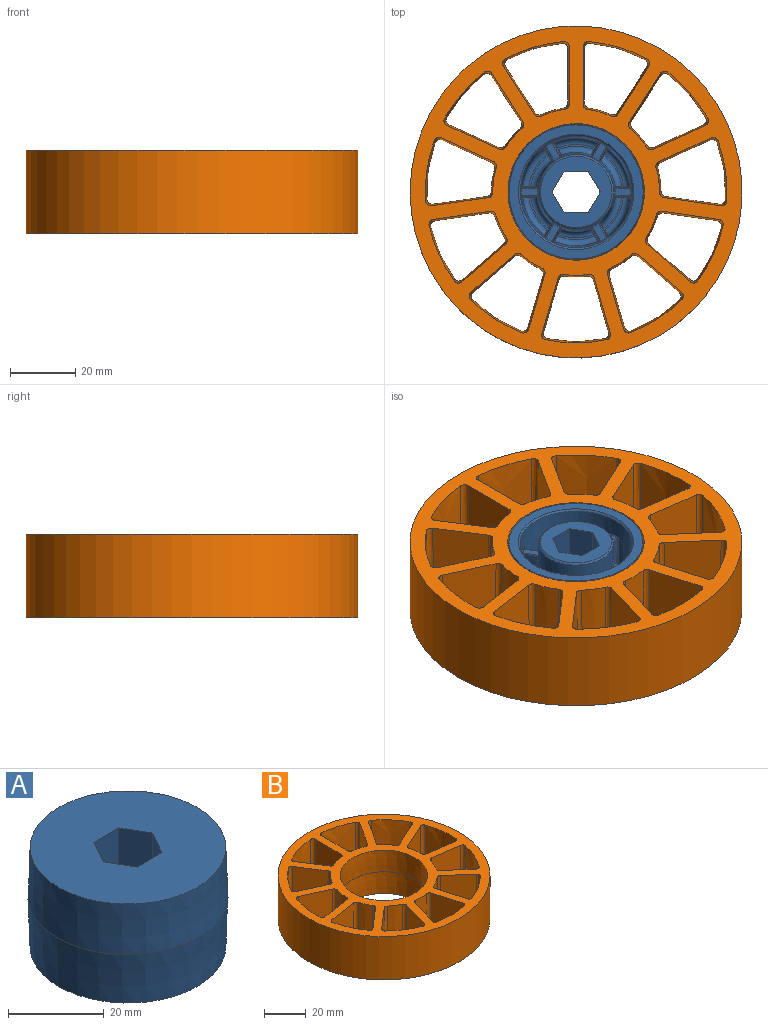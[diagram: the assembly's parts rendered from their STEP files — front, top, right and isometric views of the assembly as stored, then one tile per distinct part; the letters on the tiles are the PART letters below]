
ASSEMBLY  parts=2 mates=1
PART A: 159 faces, bbox 41.9x41.9x25.4 mm
  f0: torus R=16.68mm, axis (0,0,1), area 0.8mm2, adj f6,f31,f40,f45
  f1: torus R=11.9mm, axis (0,0,1), area 0.8mm2, adj f7,f31,f36,f41
  f2: cone r=20.24mm half-angle=2deg, axis (0,0,-1), area 1655.4mm2, adj f3,f25
  f3: cone r=20.96mm half-angle=2deg, axis (0,0,1), area 1655.4mm2, adj f2,f26
  f4: cone r=10.9mm half-angle=47deg, axis (0,0,1), area 52.3mm2, adj f7,f24
  f5: cone r=17.13mm half-angle=45deg, axis (0,0,-1), area 81.3mm2, adj f6,f26
  f6: cone r=16.46mm half-angle=2deg, axis (0,0,-1), area 1757.7mm2, adj f0,f5,f9,f12,f15,f18,f21,f27
  f7: cone r=11.43mm half-angle=2deg, axis (0,0,1), area 1163.6mm2, adj f1,f4,f8,f11,f14,f17,f20,f23
  f8: torus R=14.02mm, axis (0,0,-1), area 29mm2, adj f7,f10,f32,f146
  f9: torus R=14.55mm, axis (0,0,-1), area 37.6mm2, adj f6,f10,f35,f151
  f10: plane 9.83x5.94mm, normal (0,0,-1), area 6mm2, adj f8,f9,f33,f149
  f11: torus R=14.02mm, axis (0,0,-1), area 29mm2, adj f7,f13,f128,f135
  f12: torus R=14.55mm, axis (0,0,-1), area 37.6mm2, adj f6,f13,f133,f138
  f13: plane 11.35x1.61mm, normal (0,0,-1), area 6mm2, adj f11,f12,f131,f136
  f14: torus R=14.02mm, axis (0,0,-1), area 29mm2, adj f7,f16,f110,f117
  f15: torus R=14.55mm, axis (0,0,-1), area 37.6mm2, adj f6,f16,f115,f120
  f16: plane 9.83x5.94mm, normal (0,0,-1), area 6mm2, adj f14,f15,f113,f118
  f17: torus R=14.02mm, axis (0,0,-1), area 29mm2, adj f7,f19,f92,f99
  f18: torus R=14.55mm, axis (0,0,-1), area 37.6mm2, adj f6,f19,f97,f102
  f19: plane 9.83x5.94mm, normal (0,0,-1), area 6mm2, adj f17,f18,f95,f100
  f20: torus R=14.02mm, axis (0,0,-1), area 29mm2, adj f7,f22,f74,f81
  f21: torus R=14.55mm, axis (0,0,-1), area 37.6mm2, adj f6,f22,f79,f84
  f22: plane 11.35x1.61mm, normal (0,0,-1), area 6mm2, adj f20,f21,f77,f82
  f23: torus R=14.02mm, axis (0,0,-1), area 29mm2, adj f7,f28,f42,f63
  f24: plane 21.81x21.81mm, normal (0,0,-1), area 232.7mm2, adj f4,f153,f154,f155,f156,f157,f158
  f25: plane 41.02x41.02mm, normal (0,0,1), area 1180.9mm2, adj f2,f153,f154,f155,f156,f157,f158
  f26: plane 41.02x41.02mm, normal (0,0,-1), area 342.7mm2, adj f3,f5
  f27: torus R=14.55mm, axis (0,0,-1), area 37.6mm2, adj f6,f28,f46,f66
  f28: plane 9.83x5.94mm, normal (0,0,-1), area 6mm2, adj f23,f27,f44,f64
  f29: plane 14.75x4.78mm, normal (0,-1,-0.02), area 61.7mm2, adj f39,f42,f43,f44,f46,f47
  f30: plane 14.74x4.78mm, normal (0,1,-0.02), area 61.7mm2, adj f32,f33,f34,f35,f37,f38
  f31: plane 4.82x2.04mm, normal (0,0,-1), area 9.8mm2, adj f0,f1,f38,f43
  f32: bspline ~1.91x1.84mm, area 1mm2, adj f8,f30,f33,f34
  f33: cylinder r=0.25mm len=0.53mm, axis (-1,0,0), area 0.2mm2, adj f10,f30,f32,f35
  f34: bspline ~13.15x0.68mm, area 4.8mm2, adj f7,f30,f32,f36
  f35: bspline ~1.95x1.85mm, area 1.2mm2, adj f9,f30,f33,f37
  f36: bspline ~0.5x0.5mm, area 0.2mm2, adj f1,f7,f34,f38
  f37: bspline ~13.15x0.74mm, area 5.6mm2, adj f6,f30,f35,f40
  f38: cylinder r=0.25mm len=4.83mm, axis (-1,0,0), area 1.9mm2, adj f30,f31,f36,f40
  f39: cylinder r=0.25mm len=13.15mm, axis (0.03,-0.02,1), area 4.8mm2, adj f7,f29,f41,f42
  f40: bspline ~0.53x0.51mm, area 0.2mm2, adj f0,f6,f37,f38
  f41: bspline ~0.5x0.5mm, area 0.2mm2, adj f1,f7,f39,f43
  f42: bspline ~1.91x1.84mm, area 1mm2, adj f23,f29,f39,f44
  f43: cylinder r=0.25mm len=4.83mm, axis (1,0,0), area 1.9mm2, adj f29,f31,f41,f45
  f44: cylinder r=0.25mm len=0.53mm, axis (1,0,0), area 0.2mm2, adj f28,f29,f42,f46
  f45: bspline ~0.53x0.51mm, area 0.2mm2, adj f0,f6,f43,f47
  f46: bspline ~1.95x1.85mm, area 1.2mm2, adj f27,f29,f44,f47
  f47: bspline ~13.15x0.74mm, area 5.6mm2, adj f6,f29,f45,f46
  f48: plane 14.75x4.14mm, normal (-0.87,-0.5,-0.02), area 61.7mm2, adj f71,f74,f76,f77,f79,f80
  f49: plane 14.74x4.14mm, normal (0.87,0.5,-0.02), area 61.7mm2, adj f63,f64,f65,f66,f68,f69
  f50: plane 5.17x4.16mm, normal (0,0,-1), area 9.8mm2, adj f69,f70,f75,f76
  f51: plane 14.75x4.14mm, normal (-0.87,0.5,-0.02), area 61.7mm2, adj f89,f92,f94,f95,f97,f98
  f52: plane 14.74x4.14mm, normal (0.87,-0.5,-0.02), area 61.7mm2, adj f81,f82,f83,f84,f86,f87
  f53: plane 5.17x4.16mm, normal (0,0,-1), area 9.8mm2, adj f87,f88,f93,f94
  f54: plane 14.75x4.78mm, normal (0,1,-0.02), area 61.7mm2, adj f107,f110,f112,f113,f115,f116
  f55: plane 14.74x4.78mm, normal (0,-1,-0.02), area 61.7mm2, adj f99,f100,f101,f102,f104,f105
  f56: plane 4.82x2.04mm, normal (0,0,-1), area 9.8mm2, adj f105,f106,f111,f112
  f57: plane 14.75x4.14mm, normal (0.87,0.5,-0.02), area 61.7mm2, adj f125,f128,f130,f131,f133,f134
  f58: plane 14.74x4.14mm, normal (-0.87,-0.5,-0.02), area 61.7mm2, adj f117,f118,f119,f120,f122,f123
  f59: plane 5.17x4.16mm, normal (0,0,-1), area 9.8mm2, adj f123,f124,f129,f130
  f60: plane 14.75x4.14mm, normal (0.87,-0.5,-0.02), area 61.7mm2, adj f143,f146,f148,f149,f151,f152
  f61: plane 14.74x4.14mm, normal (-0.87,0.5,-0.02), area 61.7mm2, adj f135,f136,f137,f138,f140,f141
  f62: plane 5.17x4.16mm, normal (0,0,-1), area 9.8mm2, adj f141,f142,f147,f148
  f63: bspline ~1.84x1.75mm, area 1mm2, adj f23,f49,f64,f65
  f64: cylinder r=0.25mm len=0.59mm, axis (-0.5,0.87,0), area 0.2mm2, adj f28,f49,f63,f66
  f65: bspline ~13.15x0.59mm, area 4.8mm2, adj f7,f49,f63,f67
  f66: bspline ~1.85x1.83mm, area 1.2mm2, adj f27,f49,f64,f68
  f67: bspline ~0.5x0.49mm, area 0.2mm2, adj f7,f65,f69,f70
  f68: bspline ~13.15x0.66mm, area 5.6mm2, adj f6,f49,f66,f72
  f69: cylinder r=0.25mm len=4.31mm, axis (-0.5,0.87,0), area 1.9mm2, adj f49,f50,f67,f72
  f70: torus R=11.9mm, axis (0,0,1), area 0.8mm2, adj f7,f50,f67,f73
  f71: cylinder r=0.25mm len=13.15mm, axis (0,-0.04,1), area 4.8mm2, adj f7,f48,f73,f74
  f72: bspline ~0.56x0.51mm, area 0.2mm2, adj f6,f68,f69,f75
  f73: bspline ~0.56x0.5mm, area 0.2mm2, adj f7,f70,f71,f76
  f74: bspline ~1.84x1.77mm, area 1mm2, adj f20,f48,f71,f77
  f75: torus R=16.68mm, axis (0,0,1), area 0.8mm2, adj f6,f50,f72,f78
  f76: cylinder r=0.25mm len=4.31mm, axis (0.5,-0.87,0), area 1.9mm2, adj f48,f50,f73,f78
  f77: cylinder r=0.25mm len=0.59mm, axis (0.5,-0.87,0), area 0.2mm2, adj f22,f48,f74,f79
  f78: bspline ~0.51x0.48mm, area 0.2mm2, adj f6,f75,f76,f80
  f79: bspline ~1.85x1.79mm, area 1.2mm2, adj f21,f48,f77,f80
  f80: bspline ~13.16x0.7mm, area 5.6mm2, adj f6,f48,f78,f79
  f81: bspline ~1.84x1.77mm, area 1mm2, adj f20,f52,f82,f83
  f82: cylinder r=0.25mm len=0.59mm, axis (-0.5,-0.87,0), area 0.2mm2, adj f22,f52,f81,f84
  f83: bspline ~13.15x0.61mm, area 4.8mm2, adj f7,f52,f81,f85
  f84: bspline ~1.85x1.79mm, area 1.2mm2, adj f21,f52,f82,f86
  f85: bspline ~0.56x0.5mm, area 0.2mm2, adj f7,f83,f87,f88
  f86: bspline ~13.15x0.66mm, area 5.6mm2, adj f6,f52,f84,f90
  f87: cylinder r=0.25mm len=4.31mm, axis (0.5,0.87,0), area 1.9mm2, adj f52,f53,f85,f90
  f88: torus R=11.9mm, axis (0,0,1), area 0.8mm2, adj f7,f53,f85,f91
  f89: cylinder r=0.25mm len=13.15mm, axis (-0.03,-0.02,1), area 4.8mm2, adj f7,f51,f91,f92
  f90: bspline ~0.51x0.48mm, area 0.2mm2, adj f6,f86,f87,f93
  f91: bspline ~0.5x0.49mm, area 0.2mm2, adj f7,f88,f89,f94
  f92: bspline ~1.84x1.75mm, area 1mm2, adj f17,f51,f89,f95
  f93: torus R=16.68mm, axis (0,0,1), area 0.8mm2, adj f6,f53,f90,f96
  f94: cylinder r=0.25mm len=4.31mm, axis (-0.5,-0.87,0), area 1.9mm2, adj f51,f53,f91,f96
  f95: cylinder r=0.25mm len=0.59mm, axis (0.5,0.87,0), area 0.2mm2, adj f19,f51,f92,f97
  f96: bspline ~0.56x0.51mm, area 0.2mm2, adj f6,f93,f94,f98
  f97: bspline ~1.85x1.83mm, area 1.2mm2, adj f18,f51,f95,f98
  f98: bspline ~13.15x0.66mm, area 5.6mm2, adj f6,f51,f96,f97
  f99: bspline ~1.91x1.84mm, area 1mm2, adj f17,f55,f100,f101
  f100: cylinder r=0.25mm len=0.53mm, axis (-1,0,0), area 0.2mm2, adj f19,f55,f99,f102
  f101: bspline ~13.15x0.68mm, area 4.8mm2, adj f7,f55,f99,f103
  f102: bspline ~1.95x1.85mm, area 1.2mm2, adj f18,f55,f100,f104
  f103: bspline ~0.5x0.5mm, area 0.2mm2, adj f7,f101,f105,f106
  f104: bspline ~13.15x0.74mm, area 5.6mm2, adj f6,f55,f102,f108
  f105: cylinder r=0.25mm len=4.83mm, axis (1,0,0), area 1.9mm2, adj f55,f56,f103,f108
  f106: torus R=11.9mm, axis (0,0,1), area 0.8mm2, adj f7,f56,f103,f109
  f107: cylinder r=0.25mm len=13.15mm, axis (-0.03,0.02,1), area 4.8mm2, adj f7,f54,f109,f110
  f108: bspline ~0.53x0.51mm, area 0.2mm2, adj f6,f104,f105,f111
  f109: bspline ~0.5x0.5mm, area 0.2mm2, adj f7,f106,f107,f112
  f110: bspline ~1.91x1.84mm, area 1mm2, adj f14,f54,f107,f113
  f111: torus R=16.68mm, axis (0,0,1), area 0.8mm2, adj f6,f56,f108,f114
  f112: cylinder r=0.25mm len=4.83mm, axis (-1,0,0), area 1.9mm2, adj f54,f56,f109,f114
  f113: cylinder r=0.25mm len=0.53mm, axis (1,0,0), area 0.2mm2, adj f16,f54,f110,f115
  f114: bspline ~0.53x0.51mm, area 0.2mm2, adj f6,f111,f112,f116
  f115: bspline ~1.95x1.85mm, area 1.2mm2, adj f15,f54,f113,f116
  f116: bspline ~13.15x0.74mm, area 5.6mm2, adj f6,f54,f114,f115
  f117: bspline ~1.84x1.75mm, area 1mm2, adj f14,f58,f118,f119
  f118: cylinder r=0.25mm len=0.59mm, axis (-0.5,0.87,0), area 0.2mm2, adj f16,f58,f117,f120
  f119: bspline ~13.15x0.59mm, area 4.8mm2, adj f7,f58,f117,f121
  f120: bspline ~1.85x1.83mm, area 1.2mm2, adj f15,f58,f118,f122
  f121: bspline ~0.5x0.49mm, area 0.2mm2, adj f7,f119,f123,f124
  f122: bspline ~13.15x0.66mm, area 5.6mm2, adj f6,f58,f120,f126
  f123: cylinder r=0.25mm len=4.31mm, axis (0.5,-0.87,0), area 1.9mm2, adj f58,f59,f121,f126
  f124: torus R=11.9mm, axis (0,0,1), area 0.8mm2, adj f7,f59,f121,f127
  f125: cylinder r=0.25mm len=13.15mm, axis (0,0.04,1), area 4.8mm2, adj f7,f57,f127,f128
  f126: bspline ~0.56x0.51mm, area 0.2mm2, adj f6,f122,f123,f129
  f127: bspline ~0.56x0.5mm, area 0.2mm2, adj f7,f124,f125,f130
  f128: bspline ~1.84x1.77mm, area 1mm2, adj f11,f57,f125,f131
  f129: torus R=16.68mm, axis (0,0,1), area 0.8mm2, adj f6,f59,f126,f132
  f130: cylinder r=0.25mm len=4.31mm, axis (-0.5,0.87,0), area 1.9mm2, adj f57,f59,f127,f132
  f131: cylinder r=0.25mm len=0.59mm, axis (0.5,-0.87,0), area 0.2mm2, adj f13,f57,f128,f133
  f132: bspline ~0.51x0.48mm, area 0.2mm2, adj f6,f129,f130,f134
  f133: bspline ~1.85x1.79mm, area 1.2mm2, adj f12,f57,f131,f134
  f134: bspline ~13.16x0.7mm, area 5.6mm2, adj f6,f57,f132,f133
  f135: bspline ~1.84x1.77mm, area 1mm2, adj f11,f61,f136,f137
  f136: cylinder r=0.25mm len=0.59mm, axis (0.5,0.87,0), area 0.2mm2, adj f13,f61,f135,f138
  f137: bspline ~13.15x0.68mm, area 4.8mm2, adj f7,f61,f135,f139
  f138: bspline ~1.85x1.79mm, area 1.2mm2, adj f12,f61,f136,f140
  f139: bspline ~0.56x0.5mm, area 0.2mm2, adj f7,f137,f141,f142
  f140: bspline ~13.15x0.66mm, area 5.6mm2, adj f6,f61,f138,f144
  f141: cylinder r=0.25mm len=4.31mm, axis (-0.5,-0.87,0), area 1.9mm2, adj f61,f62,f139,f144
  f142: torus R=11.9mm, axis (0,0,1), area 0.8mm2, adj f7,f62,f139,f145
  f143: cylinder r=0.25mm len=13.15mm, axis (0.03,0.02,1), area 4.8mm2, adj f7,f60,f145,f146
  f144: bspline ~0.51x0.48mm, area 0.2mm2, adj f6,f140,f141,f147
  f145: bspline ~0.5x0.49mm, area 0.2mm2, adj f7,f142,f143,f148
  f146: bspline ~1.84x1.75mm, area 1mm2, adj f8,f60,f143,f149
  f147: torus R=16.68mm, axis (0,0,1), area 0.8mm2, adj f6,f62,f144,f150
  f148: cylinder r=0.25mm len=4.31mm, axis (0.5,0.87,0), area 1.9mm2, adj f60,f62,f145,f150
  f149: cylinder r=0.25mm len=0.59mm, axis (-0.5,-0.87,0), area 0.2mm2, adj f10,f60,f146,f151
  f150: bspline ~0.56x0.51mm, area 0.2mm2, adj f6,f147,f148,f152
  f151: bspline ~1.85x1.83mm, area 1.2mm2, adj f9,f60,f149,f152
  f152: bspline ~13.15x0.66mm, area 5.6mm2, adj f6,f60,f150,f151
  f153: plane 25.4x6.38mm, normal (0.87,0.5,0), area 187mm2, adj f24,f25,f154,f158
  f154: plane 25.4x7.36mm, normal (0,1,0), area 187mm2, adj f24,f25,f153,f155
  f155: plane 25.4x6.38mm, normal (-0.87,0.5,0), area 187mm2, adj f24,f25,f154,f156
  f156: plane 25.4x6.38mm, normal (-0.87,-0.5,0), area 187mm2, adj f24,f25,f155,f157
  f157: plane 25.4x7.36mm, normal (0,-1,0), area 187mm2, adj f24,f25,f156,f158
  f158: plane 25.4x6.38mm, normal (0.87,-0.5,0), area 187mm2, adj f24,f25,f153,f157
PART B: 93 faces, bbox 101.7x101.7x25.8 mm
  f0: cylinder r=50.8mm len=101.6mm, axis (0,0,-1), area 8107.3mm2, adj f25,f27
  f1: cone r=20.96mm half-angle=0.3deg, axis (0,0,1), area 1669.7mm2, adj f2,f27
  f2: cone r=20.89mm half-angle=0.3deg, axis (0,0,-1), area 1669.7mm2, adj f1,f25
  f3: cone r=45.72mm half-angle=1deg, axis (0,0,1), area 460.8mm2, adj f25,f27,f58,f59
  f4: cone r=25.97mm half-angle=1deg, axis (0,0,-1), area 186.1mm2, adj f25,f27,f80,f81
  f5: cone r=25.97mm half-angle=1deg, axis (0,0,-1), area 186.2mm2, adj f25,f27,f88,f89
  f6: cone r=45.72mm half-angle=1deg, axis (0,0,1), area 460.8mm2, adj f25,f27,f90,f91
  f7: cone r=45.72mm half-angle=1deg, axis (0,0,1), area 460.8mm2, adj f25,f27,f82,f83
  f8: cone r=25.97mm half-angle=1deg, axis (0,0,-1), area 186.2mm2, adj f25,f27,f76,f77
  f9: cone r=45.72mm half-angle=1deg, axis (0,0,1), area 460.8mm2, adj f25,f27,f78,f79
  f10: cone r=25.97mm half-angle=1deg, axis (0,0,-1), area 186.2mm2, adj f25,f27,f72,f73
  f11: cone r=45.72mm half-angle=1deg, axis (0,0,1), area 460.8mm2, adj f25,f27,f74,f75
  f12: cone r=25.97mm half-angle=1deg, axis (0,0,-1), area 186.2mm2, adj f25,f27,f68,f69
  f13: cone r=45.72mm half-angle=1deg, axis (0,0,1), area 460.8mm2, adj f25,f27,f70,f71
  f14: cone r=25.97mm half-angle=1deg, axis (0,0,-1), area 186.2mm2, adj f25,f27,f64,f65
  f15: cone r=45.72mm half-angle=1deg, axis (0,0,1), area 460.8mm2, adj f25,f27,f66,f67
  f16: cone r=25.97mm half-angle=1deg, axis (0,0,-1), area 186.2mm2, adj f25,f27,f60,f61
  f17: cone r=45.72mm half-angle=1deg, axis (0,0,1), area 460.8mm2, adj f25,f27,f62,f63
  f18: cone r=25.97mm half-angle=1deg, axis (0,0,-1), area 186.2mm2, adj f25,f27,f56,f57
  f19: cone r=25.97mm half-angle=1deg, axis (0,0,-1), area 186.2mm2, adj f25,f27,f52,f53
  f20: cone r=45.72mm half-angle=1deg, axis (0,0,1), area 460.8mm2, adj f25,f27,f54,f55
  f21: cone r=25.97mm half-angle=1deg, axis (0,0,-1), area 186.2mm2, adj f25,f27,f49,f50
  f22: cone r=45.72mm half-angle=1deg, axis (0,0,1), area 460.8mm2, adj f25,f27,f51,f92
  f23: plane 25.4x17.56mm, normal (1,0,0.02), area 435mm2, adj f25,f27,f85,f86
  f24: plane 25.4x17.56mm, normal (-1,0,0.02), area 435mm2, adj f25,f27,f50,f92
  f25: plane 101.66x101.66mm, normal (0,0,1), area 3063.9mm2, adj f0,f2,f3,f4,f5,f6,f7,f8
  f26: cone r=25.97mm half-angle=1deg, axis (0,0,-1), area 186.2mm2, adj f25,f27,f86,f87
  f27: plane 101.66x101.66mm, normal (0,0,-1), area 3415.8mm2, adj f0,f1,f3,f4,f5,f6,f7,f8
  f28: cone r=45.72mm half-angle=1deg, axis (0,0,1), area 460.8mm2, adj f25,f27,f84,f85
  f29: plane 25.4x14.77mm, normal (0.84,0.54,0.02), area 435mm2, adj f25,f27,f49,f51
  f30: plane 25.4x14.77mm, normal (-0.84,-0.54,0.02), area 435mm2, adj f25,f27,f53,f54
  f31: plane 25.4x15.97mm, normal (0.42,0.91,0.02), area 435mm2, adj f25,f27,f52,f55
  f32: plane 25.4x15.97mm, normal (-0.42,-0.91,0.02), area 435mm2, adj f25,f27,f57,f58
  f33: plane 25.4x17.38mm, normal (-0.14,0.99,0.02), area 435mm2, adj f25,f27,f56,f59
  f34: plane 25.4x17.38mm, normal (0.14,-0.99,0.02), area 435mm2, adj f25,f27,f61,f62
  f35: plane 25.4x13.27mm, normal (-0.65,0.76,0.02), area 435mm2, adj f25,f27,f60,f63
  f36: plane 25.4x13.27mm, normal (0.65,-0.76,0.02), area 435mm2, adj f25,f27,f65,f66
  f37: plane 25.4x16.85mm, normal (-0.96,0.28,0.02), area 435mm2, adj f25,f27,f64,f67
  f38: plane 25.4x16.85mm, normal (0.96,-0.28,0.02), area 435mm2, adj f25,f27,f69,f70
  f39: plane 25.4x16.85mm, normal (-0.96,-0.28,0.02), area 435mm2, adj f25,f27,f68,f71
  f40: plane 25.4x16.85mm, normal (0.96,0.28,0.02), area 435mm2, adj f25,f27,f73,f74
  f41: plane 25.4x13.27mm, normal (-0.65,-0.76,0.02), area 435mm2, adj f25,f27,f72,f75
  f42: plane 25.4x13.27mm, normal (0.65,0.76,0.02), area 435mm2, adj f25,f27,f77,f78
  f43: plane 25.4x17.38mm, normal (-0.14,-0.99,0.02), area 435mm2, adj f25,f27,f76,f79
  f44: plane 25.4x17.38mm, normal (0.14,0.99,0.02), area 435mm2, adj f25,f27,f81,f82
  f45: plane 25.4x15.97mm, normal (0.42,-0.91,0.02), area 435mm2, adj f25,f27,f80,f83
  f46: plane 25.4x15.97mm, normal (-0.42,0.91,0.02), area 435mm2, adj f25,f27,f89,f90
  f47: plane 25.4x14.77mm, normal (0.84,-0.54,0.02), area 435mm2, adj f25,f27,f88,f91
  f48: plane 25.4x14.77mm, normal (-0.84,0.54,0.02), area 435mm2, adj f25,f27,f84,f87
  f49: bspline ~25.41x2.15mm, area 57.6mm2, adj f21,f25,f27,f29
  f50: bspline ~25.41x1.96mm, area 57.6mm2, adj f21,f24,f25,f27
  f51: bspline ~25.41x2.43mm, area 66.9mm2, adj f22,f25,f27,f29
  f52: bspline ~25.41x2.17mm, area 57.6mm2, adj f19,f25,f27,f31
  f53: bspline ~25.41x2.15mm, area 57.6mm2, adj f19,f25,f27,f30
  f54: bspline ~25.75x2.43mm, area 66.9mm2, adj f20,f25,f27,f30
  f55: bspline ~25.75x2.44mm, area 66.9mm2, adj f20,f25,f27,f31
  f56: bspline ~25.73x1.95mm, area 57.6mm2, adj f18,f25,f27,f33
  f57: bspline ~25.73x2.13mm, area 57.6mm2, adj f18,f25,f27,f32
  f58: bspline ~25.75x2.41mm, area 66.9mm2, adj f3,f25,f27,f32
  f59: bspline ~25.41x2.23mm, area 66.9mm2, adj f3,f25,f27,f33
  f60: bspline ~25.73x2.13mm, area 57.6mm2, adj f16,f25,f27,f35
  f61: bspline ~25.41x2.07mm, area 57.6mm2, adj f16,f25,f27,f34
  f62: bspline ~25.41x2.31mm, area 66.9mm2, adj f17,f25,f27,f34
  f63: bspline ~25.75x2.4mm, area 66.9mm2, adj f17,f25,f27,f35
  f64: bspline ~25.73x2.14mm, area 57.6mm2, adj f14,f25,f27,f37
  f65: bspline ~25.73x2.09mm, area 57.6mm2, adj f14,f25,f27,f36
  f66: bspline ~25.41x2.36mm, area 66.9mm2, adj f15,f25,f27,f36
  f67: bspline ~25.75x2.4mm, area 66.9mm2, adj f15,f25,f27,f37
  f68: bspline ~25.41x2.05mm, area 57.6mm2, adj f12,f25,f27,f39
  f69: bspline ~25.41x2.05mm, area 57.6mm2, adj f12,f25,f27,f38
  f70: bspline ~25.41x2.34mm, area 66.9mm2, adj f13,f25,f27,f38
  f71: bspline ~25.41x2.34mm, area 66.9mm2, adj f13,f25,f27,f39
  f72: bspline ~25.73x2.09mm, area 57.6mm2, adj f10,f25,f27,f41
  f73: bspline ~25.73x2.14mm, area 57.6mm2, adj f10,f25,f27,f40
  f74: bspline ~25.75x2.4mm, area 66.9mm2, adj f11,f25,f27,f40
  f75: bspline ~25.41x2.36mm, area 66.9mm2, adj f11,f25,f27,f41
  f76: bspline ~25.41x2.07mm, area 57.6mm2, adj f8,f25,f27,f43
  f77: bspline ~25.73x2.13mm, area 57.6mm2, adj f8,f25,f27,f42
  f78: bspline ~25.75x2.4mm, area 66.9mm2, adj f9,f25,f27,f42
  f79: bspline ~25.41x2.31mm, area 66.9mm2, adj f9,f25,f27,f43
  f80: bspline ~25.73x2.13mm, area 57.6mm2, adj f4,f25,f27,f45
  f81: bspline ~25.41x1.94mm, area 57.6mm2, adj f4,f25,f27,f44
  f82: bspline ~25.41x2.23mm, area 66.9mm2, adj f7,f25,f27,f44
  f83: bspline ~25.75x2.41mm, area 66.9mm2, adj f7,f25,f27,f45
  f84: bspline ~25.41x2.43mm, area 66.9mm2, adj f25,f27,f28,f48
  f85: bspline ~25.41x2.18mm, area 66.9mm2, adj f23,f25,f27,f28
  f86: bspline ~25.41x1.96mm, area 57.6mm2, adj f23,f25,f26,f27
  f87: bspline ~25.41x2.15mm, area 57.6mm2, adj f25,f26,f27,f48
  f88: bspline ~25.41x2.15mm, area 57.6mm2, adj f5,f25,f27,f47
  f89: bspline ~25.41x2.17mm, area 57.6mm2, adj f5,f25,f27,f46
  f90: bspline ~25.75x2.44mm, area 66.9mm2, adj f6,f25,f27,f46
  f91: bspline ~25.75x2.43mm, area 66.9mm2, adj f6,f25,f27,f47
  f92: bspline ~25.41x2.18mm, area 66.9mm2, adj f22,f24,f25,f27
PLACE A rot(axis=(0,-1,0),180deg) t=(-8.63,-95.98,41.98)mm
PLACE B t=(-8.63,-95.98,54.68)mm
MATE fastened A.f2 <-> B.f0  axis (0,0,-1) through (-8.63,-95.98,54.68)mm
